# Revit family: IS_ConnectSpace_E0379_BIM_DE
name_source: partatom
category: Casework
revit_build: Autodesk Revit 2015 (Build: 20140606_1530(x64)
units: mm (PartAtom-declared; Revit-internal decimal feet)

## types (3) — shared parameters
Accessories = www.idealstandard.de\ersatzteile
AreaUnits = millimeters
Assembly Code = C1030200
AssetType = Fixed
Brand = Ideal Standard
CodePerformance = FSC, EN 14749:2005
ConnectionType = Mechanical
Default Elevation = 2000 mm  [stored 6.56168 ft]
Depth = 210 mm
DurationUnit = year
ExpectedLife = 25
Features = CONNECT SPACE column 300x210mm, 2 doors
Height = 1750 mm
IfcExportAs = IfcFurnitureType
IfcExportType = Bathroom integrated furniture
InstallationInstructions = www.idealstandard.de\produkte
LinearUnits = millimeters
ManufacturerURL = www.idealstandard.com
Material = Varies, see product information
MetalMtl = ISI_IdealStandard_Furniture_Chrome2_Render
NBSDescription = Bathroom integrated furniture
NBSReference = 45-35-72/320
NominalDepth = 210 mm
NominalHeight = 1750 mm
NominalLength = 210 mm
NominalWidth = 300 mm
ProductInformation = www.idealstandard.de/produkte
Shape = Rectangular
Size = 1750 x 210 x 300 mm
Space = Internal
SpareParts = www.idealstandard.de/ersatzteile
Style = Bathroom cabinets
SustainabilityPerformance = FSC
URL = www.idealstandard.com
Uniclass2015Code = Pr_40_30_78_03
Uniclass2015Title = Bathroom cabinets
Uniclass2015Version = Products v1.1
Version = 2
VolumeUnits = Litres
WarrantyDurationUnit = year
Width = 300 mm
zero-valued in all types: Cost

## per-type parameters (varying)
| type | BIMObjectName | BarCode | Color | Description | Finish | LaminateMtl | MainColor | Model | ModelNumber | ModelReference | Name | NettWeight |
| E0412WG - Concept Space 300 x 200 mm  - Tall Unit - 2Door - Gloss White | ISI_IdealStandard_BathroomIntegratedFurniture_ConnectSpace_E0412WG | 5017830455523 | Gloss White | E0379WG CONNECT SPACE column 300x210mm, 2 doors | Gloss White | ISI_IdealStandard_Laminate_Furniture_GlossWhite_Render | Gloss White | E0379WG | E0379WG | E0379WG CONNECT SPACE column 300x210mm, 2 doors | BathroomIntegratedFurniture_ConnectSpace_E0412WG_IdealStandard | 21 Kg |
| E0412KS - Concept Space 300 x 200 mm  - Tall Unit - 2Door - Elm | ISI_IdealStandard_BathroomIntegratedFurniture_ConnectSpace_E0412KS | 5017830455493 | Elm | E0379KS CONNECT SPACE column 300x210mm, 2 doors | Elm | ISI_IdealStandard_Laminate_Furniture_Elm_Render | Elm | E0379KS | E0379KS | E0379KS CONNECT SPACE column 300x210mm, 2 doors | BathroomIntegratedFurniture_ConnectSpace_E0412KS_IdealStandard | 21 Kg |
| E0412KR - Concept Space 300 x 200 mm  - Tall Unit - 2Door - Dark Grey | ISI_IdealStandard_BathroomIntegratedFurniture_ConnectSpace_E0412KR | 5017830455486 | Gloss Grey | E0379KR CONNECT SPACE column 300x210mm, 2 doors | Gloss Grey | ISI_IdealStandard_Laminate_Furniture_DarkGrey_Render | Gloss Grey | E0379KR | E0379KR | E0379KR CONNECT SPACE column 300x210mm, 2 doors | BathroomIntegratedFurniture_ConnectSpace_E0412KR_IdealStandard | 22 Kg |

note: [stored X ft] marks values corroborated as IEEE doubles in the binary element streams (Revit-internal decimal feet)

## geometry (parser evidence)
native form markers: Blend x2, Sweep x3
no freeform markers — native parametric forms only
